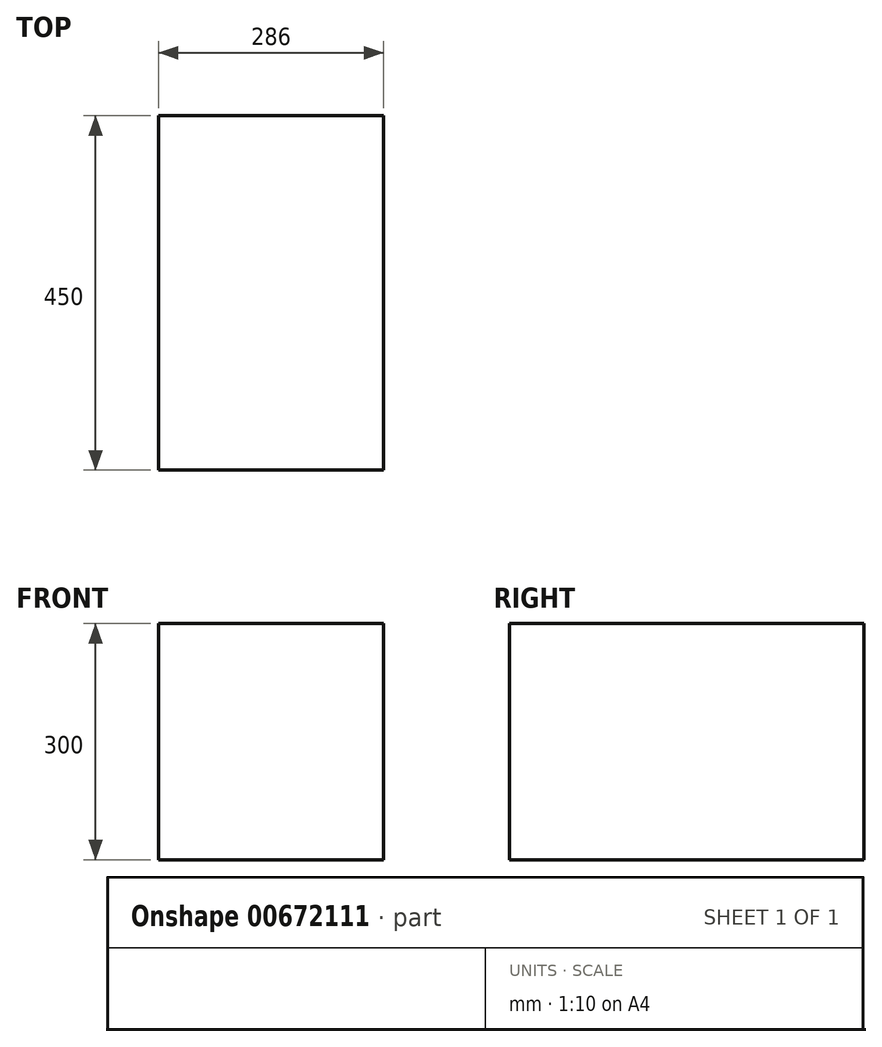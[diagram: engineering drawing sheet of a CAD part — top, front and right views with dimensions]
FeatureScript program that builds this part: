
annotation { "Feature Type Name" : "Feature", "Feature Type Description" : "" }
export const myFeature = defineFeature(function(context is Context, id is Id, definition is map)
    precondition{}
    {
        {
            var Q0;
            Q0=qCreatedBy(makeId("Front.planeOp"),FACE);
            var sketch = newSketch(context, id + "F0", { "sketchPlane" : qUnion([Q0])});
            skLineSegment(sketch, "E0.bottom", {"start": v(-138.48, 215.37) * mm, "end": v(147.52, 215.37) * mm});
            skLineSegment(sketch, "E0.top", {"start": v(-138.48, -84.63) * mm, "end": v(147.52, -84.63) * mm});
            skLineSegment(sketch, "E0.left", {"start": v(-138.48, 215.37) * mm, "end": v(-138.48, -84.63) * mm});
            skLineSegment(sketch, "E0.right", {"start": v(147.52, 215.37) * mm, "end": v(147.52, -84.63) * mm});
            skSolve(sketch);
        }
        {
            var Q0;
            Q0=qSketchRegion(id+"F0",true);
            extrude(context, id + "F1", {"entities" : qUnion([Q0]), "oppositeDirection" : true, "depth" : 450 * mm, "offsetDistance" : 25 * mm});
        }
        {
            var Q0;
            Q0=makeQuery(id+"F1.opExtrude","SWEPT_FACE",FACE,{"disambiguationData":[OSD([sQuery(id+"F0.wireOp",EDGE,"E0.bottom")])]});
            var sketch = newSketch(context, id + "F2", { "sketchPlane" : qUnion([Q0])});
            skLineSegment(sketch, "E1.bottom", {"start": v(-123.48, 435) * mm, "end": v(132.52, 435) * mm});
            skLineSegment(sketch, "E1.top", {"start": v(-123.48, 15) * mm, "end": v(132.52, 15) * mm});
            skLineSegment(sketch, "E1.left", {"start": v(-123.48, 435) * mm, "end": v(-123.48, 15) * mm});
            skLineSegment(sketch, "E1.right", {"start": v(132.52, 435) * mm, "end": v(132.52, 15) * mm});
            skSolve(sketch);
        }
        {
            var Q0;
            Q0 = qSketchRegion(id + "F2", true);
            extrude(context, id + "F3", {"entities" : qUnion([Q0]), "operationType" : NewBodyOperationType.ADD, "oppositeDirection" : true, "depth" : 285 * mm, "offsetDistance" : 25 * mm});
        }
    });
